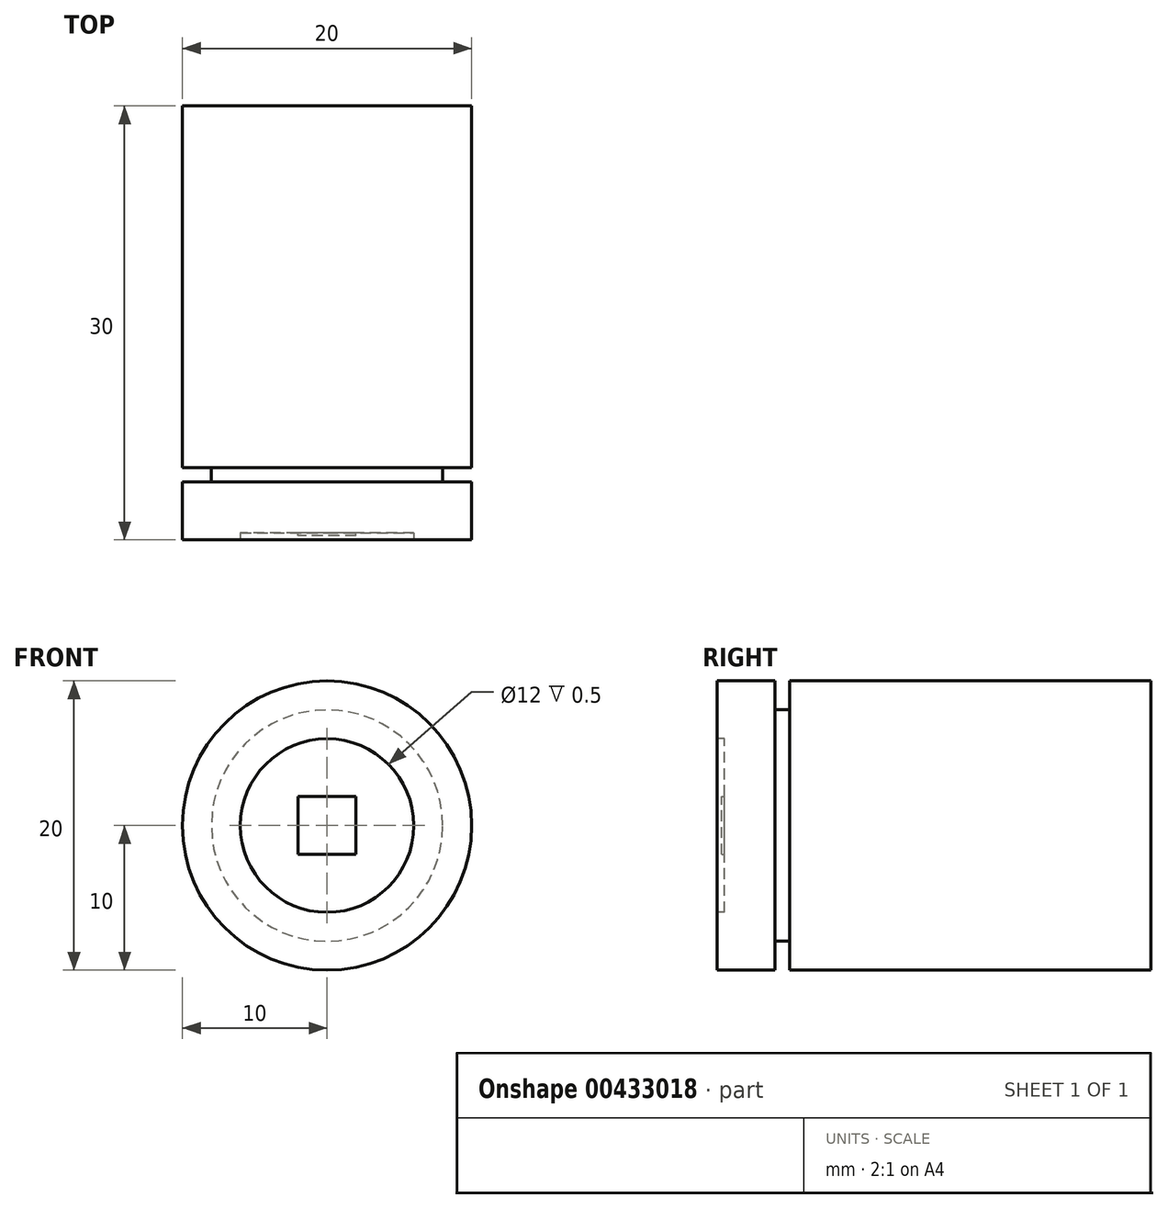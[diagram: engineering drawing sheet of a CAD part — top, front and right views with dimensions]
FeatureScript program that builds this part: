
annotation { "Feature Type Name" : "Feature", "Feature Type Description" : "" }
export const myFeature = defineFeature(function(context is Context, id is Id, definition is map)
    precondition{}
    {
        {
            var Q0;
            Q0=qCreatedBy(makeId("Front.planeOp"),FACE);
            var sketch = newSketch(context, id + "F0", { "sketchPlane" : qUnion([Q0])});
            skCircle(sketch, "E0", {"center": v(0, 0) * mm, "radius": 10 * mm});
            skSolve(sketch);
        }
        {
            var Q0;
            Q0 = qSketchRegion(id + "F0", true);
            var Q1;
            Q1=makeQuery(id+"F0.imprint","IMPRINT",FACE,{"disambiguationData":[TD([[makeQuery(id+"F0.imprint","IMPRINT",EDGE,{"derivedFrom":sQuery(id+"F0.wireOp",EDGE,"E0")}),1.0]])]});
            extrude(context, id + "F1", {"entities" : qUnion([Q0, Q1]), "depth" : 25 * mm, "offsetDistance" : 25 * mm});
        }
        {
            var Q0;
            Q0=makeQuery(id+"F1.opExtrude","CAP_FACE",FACE,{"disambiguationData":[OSD([sQuery(id+"F0.wireOp",EDGE,"E0")])],"isStart":false});
            var sketch = newSketch(context, id + "F2", { "sketchPlane" : qUnion([Q0])});
            skCircle(sketch, "E1.0", {"center": v(0, 0) * mm, "radius": 8 * mm});
            skSolve(sketch);
        }
        {
            var Q0;
            Q0=makeQuery(id+"F2.imprint","IMPRINT",FACE,{"disambiguationData":[TD([[makeQuery(id+"F2.imprint","IMPRINT",EDGE,{"derivedFrom":sQuery(id+"F2.wireOp",EDGE,"E1.0")}),1.0]])]});
            extrude(context, id + "F3", {"entities" : qUnion([Q0]), "operationType" : NewBodyOperationType.ADD, "depth" : 1 * mm, "offsetDistance" : 25 * mm});
        }
        {
            var Q0;
            Q0=makeQuery(id+"F3.opExtrude","CAP_FACE",FACE,{"disambiguationData":[OSD([sQuery(id+"F2.wireOp",EDGE,"E1.0")])],"isStart":false});
            var sketch = newSketch(context, id + "F4", { "sketchPlane" : qUnion([Q0])});
            skCircle(sketch, "E2.0", {"center": v(0, 0) * mm, "radius": 10 * mm});
            skSolve(sketch);
        }
        {
            var Q0;
            Q0=makeQuery(id+"F4.imprint","IMPRINT",FACE,{"disambiguationData":[TD([[makeQuery(id+"F4.imprint","IMPRINT",EDGE,{"derivedFrom":makeQuery(id+"F3.opExtrude","CAP_EDGE",EDGE,{"disambiguationData":[OSD([sQuery(id+"F2.wireOp",EDGE,"E1.0")])],"isStart":false})}),1.0]])]});
            var Q1;
            Q1=makeQuery(id+"F4.imprint","IMPRINT",FACE,{"disambiguationData":[TD([[makeQuery(id+"F4.imprint","IMPRINT",EDGE,{"derivedFrom":sQuery(id+"F4.wireOp",EDGE,"E2.0")}),1.0]])]});
            extrude(context, id + "F5", {"entities" : qUnion([Q0, Q1]), "operationType" : NewBodyOperationType.ADD, "depth" : 4 * mm, "offsetDistance" : 25 * mm});
        }
        {
            var Q0;
            Q0=makeQuery(id+"F5.opExtrude","CAP_FACE",FACE,{"disambiguationData":[OSD([sQuery(id+"F4.wireOp",EDGE,"E2.0")])],"isStart":false});
            var sketch = newSketch(context, id + "F6", { "sketchPlane" : qUnion([Q0])});
            skCircle(sketch, "E3.0", {"center": v(0, 0) * mm, "radius": 6 * mm});
            skSolve(sketch);
        }
        {
            var Q0;
            Q0=makeQuery(id+"F6.imprint","IMPRINT",FACE,{"disambiguationData":[TD([[makeQuery(id+"F6.imprint","IMPRINT",EDGE,{"derivedFrom":sQuery(id+"F6.wireOp",EDGE,"E3.0")}),1.0]])]});
            extrude(context, id + "F7", {"entities" : qUnion([Q0]), "operationType" : NewBodyOperationType.REMOVE, "oppositeDirection" : true, "depth" : 0.5 * mm, "offsetDistance" : 25 * mm});
        }
        {
            var Q0;
            Q0=makeQuery(id+"F7.boolean.opBoolean","COPY",FACE,{"derivedFrom":makeQuery(id+"F7.opExtrude","CAP_FACE",FACE,{"disambiguationData":[OSD([sQuery(id+"F6.wireOp",EDGE,"E3.0")])],"isStart":false})});
            var sketch = newSketch(context, id + "F8", { "sketchPlane" : qUnion([Q0])});
            skLineSegment(sketch, "E4.bottom", {"start": v(2, -2) * mm, "end": v(-2, -2) * mm});
            skLineSegment(sketch, "E4.top", {"start": v(2, 2) * mm, "end": v(-2, 2) * mm});
            skLineSegment(sketch, "E4.left", {"start": v(2, -2) * mm, "end": v(2, 2) * mm});
            skLineSegment(sketch, "E4.right", {"start": v(-2, -2) * mm, "end": v(-2, 2) * mm});
            skPoint(sketch, "E4.middle", {"position": v(0, 0) * mm});
            skSolve(sketch);
        }
        {
            var Q0;
            Q0=makeQuery(id+"F8.imprint","IMPRINT",FACE,{"disambiguationData":[TD([[makeQuery(id+"F8.imprint","IMPRINT",EDGE,{"derivedFrom":sQuery(id+"F8.wireOp",EDGE,"E4.bottom")}),-1.0]])]});
            extrude(context, id + "F9", {"entities" : qUnion([Q0]), "depth" : 0.2 * mm, "offsetDistance" : 25 * mm});
        }
    });
